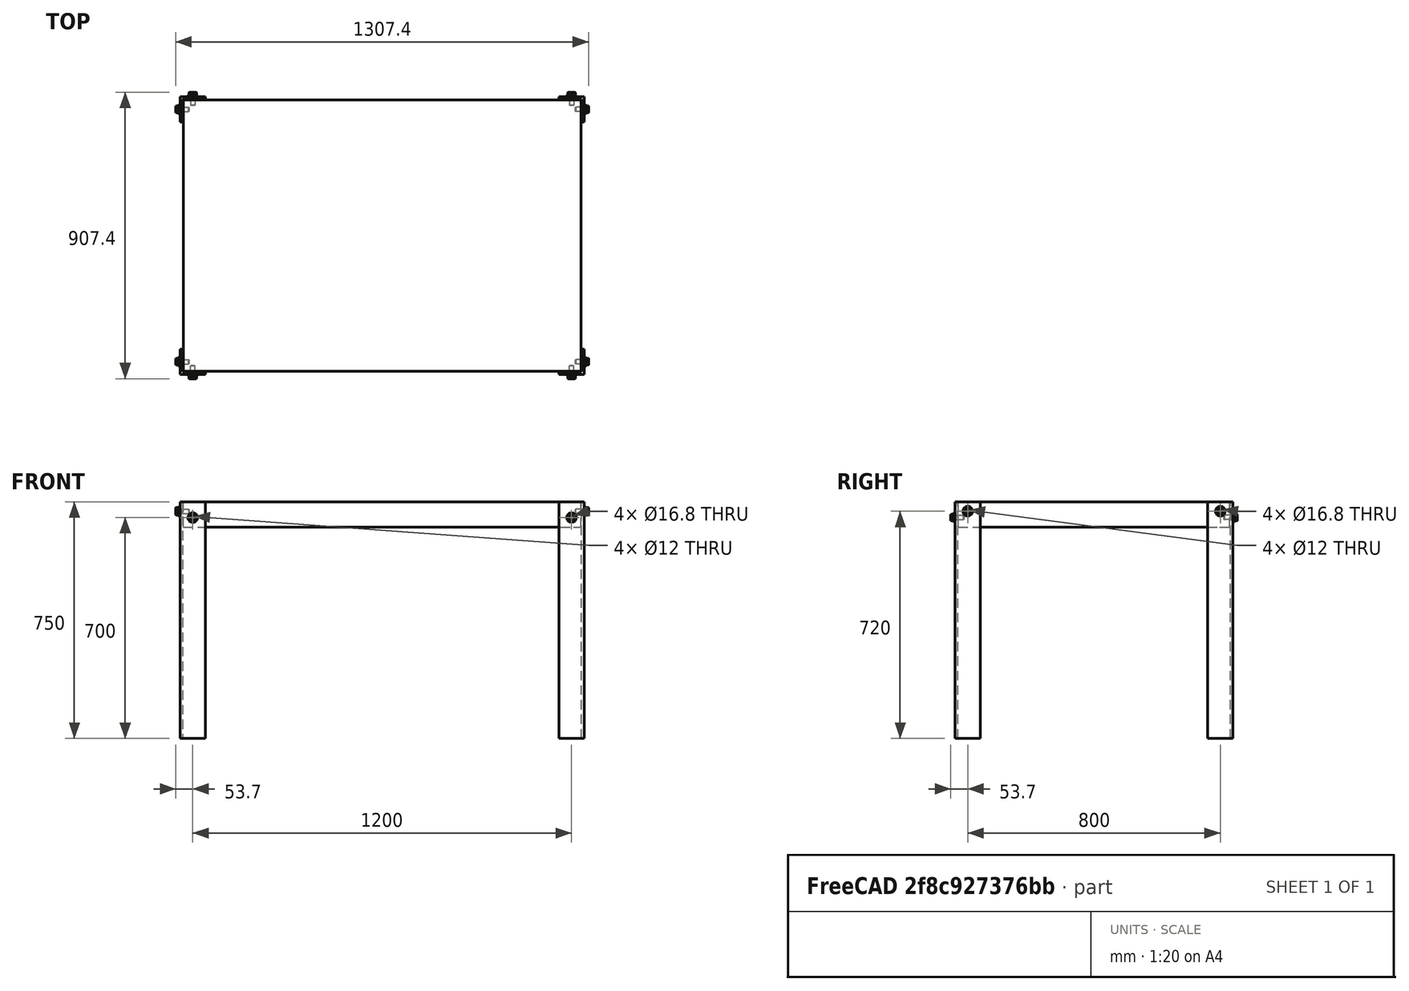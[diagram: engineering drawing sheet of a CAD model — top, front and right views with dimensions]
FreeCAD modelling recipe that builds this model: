
FCSTD DOCUMENT  (FreeCAD 0.17R13519 (Git))
Label: test005_table
License: All rights reserved
LicenseURL: http://en.wikipedia.org/wiki/All_rights_reserved
objects: Part::Cut×12, Part::Box×9, Part::FeaturePython×8, Part::Cylinder×4, App::DocumentObjectGroup×1
note: 33 computed .brp shape members not serialized (recipe doc carries the construction recipe); baked Part::Feature solids carry a one-line shape summary decoded from their .brp

FEATURE [Part::Box] Box  label="Cube"
  AttacherType = Attacher::AttachEngine3D
  Height = 750
  Length = 80
  Width = 80
FEATURE [Part::Box] Box001  label="Cube001"
  AttacherType = Attacher::AttachEngine3D
  Height = 750
  Length = 80
  Placement = pos=(8,8,0) rot=(0,0,1;0rad)
  Width = 80
FEATURE [Part::Cut] Cut
  Base = -> Box
  Tool = -> Box001
FEATURE [Part::Box] Box002  label="Cube002"
  AttacherType = Attacher::AttachEngine3D
  Height = 750
  Length = 80
  Placement = pos=(0,800,0) rot=(0,0,1;0rad)
  Width = 80
FEATURE [Part::Box] Box003  label="Cube003"
  AttacherType = Attacher::AttachEngine3D
  Height = 750
  Length = 80
  Placement = pos=(8,792,0) rot=(0,0,1;0rad)
  Width = 80
FEATURE [Part::Cut] Cut001
  Base = -> Box002
  Tool = -> Box003
FEATURE [Part::Box] Box004  label="Cube004"
  AttacherType = Attacher::AttachEngine3D
  Height = 750
  Length = 80
  Placement = pos=(1200,0,0) rot=(0,0,1;0rad)
  Width = 80
FEATURE [Part::Box] Box005  label="Cube005"
  AttacherType = Attacher::AttachEngine3D
  Height = 750
  Length = 80
  Placement = pos=(1192,8,0) rot=(0,0,1;0rad)
  Width = 80
FEATURE [Part::Cut] Cut002
  Base = -> Box004
  Tool = -> Box005
FEATURE [Part::Box] Box006  label="Cube006"
  AttacherType = Attacher::AttachEngine3D
  Height = 750
  Length = 80
  Placement = pos=(1200,800,0) rot=(0,0,1;0rad)
  Width = 80
FEATURE [Part::Box] Box007  label="Cube007"
  AttacherType = Attacher::AttachEngine3D
  Height = 750
  Length = 80
  Placement = pos=(1192,792,0) rot=(0,0,1;0rad)
  Width = 80
FEATURE [Part::Cut] Cut003
  Base = -> Box006
  Tool = -> Box007
FEATURE [Part::Cylinder] Cylinder
  Angle = 360
  AttacherType = Attacher::AttachEngine3D
  Height = 1300
  Placement = pos=(-10,40,720) rot=(0,1,0;1.5708rad)
  Radius = 6
FEATURE [Part::Cylinder] Cylinder001
  Angle = 360
  AttacherType = Attacher::AttachEngine3D
  Height = 1300
  Placement = pos=(-10,840,720) rot=(0,1,0;1.5708rad)
  Radius = 6
FEATURE [Part::Cylinder] Cylinder002
  Angle = 360
  AttacherType = Attacher::AttachEngine3D
  Height = 900
  Placement = pos=(40,-10,700) rot=(-1,0,0;1.5708rad)
  Radius = 6
FEATURE [Part::Cylinder] Cylinder003
  Angle = 360
  AttacherType = Attacher::AttachEngine3D
  Height = 900
  Placement = pos=(1240,-10,700) rot=(-1,0,0;1.5708rad)
  Radius = 6
FEATURE [Part::Cut] Cut004
  Base = -> Cut
  Tool = -> Cylinder
FEATURE [Part::Cut] Cut005
  Base = -> Cut002
  Tool = -> Cylinder
FEATURE [Part::Cut] Cut006
  Base = -> Cut001
  Tool = -> Cylinder001
FEATURE [Part::Cut] Cut007  label="LeftBackLeg"
  Base = -> Cut006
  Tool = -> Cylinder002
FEATURE [Part::Cut] Cut008  label="RightFrontLeg"
  Base = -> Cut005
  Tool = -> Cylinder003
FEATURE [Part::Cut] Cut009
  Base = -> Cut003
  Tool = -> Cylinder003
FEATURE [Part::Cut] Cut010  label="RightBackLeg"
  Base = -> Cut009
  Tool = -> Cylinder001
FEATURE [Part::Cut] Cut011  label="LeftFrontLeg"
  Base = -> Cut004
  Tool = -> Cylinder002
FEATURE [Part::Box] Box008  label="Table"
  AttacherType = Attacher::AttachEngine3D
  Height = 80
  Length = 1260
  Placement = pos=(10,10,670) rot=(0,0,1;0rad)
  Width = 860
FEATURE [Part::FeaturePython] Screw  label="(M14)x30-Screw"  # Fasteners workbench fastener (typed FeaturePython)
  Placement = pos=(40,-2,700) rot=(1,0,0;1.5708rad)
  baseObject = -> Cut011 [Edge9]
  diameter = 6
  invert = true
  length = 0
  matchOuter = false
  offset = 2
  thread = false
  type = 2
FEATURE [Part::FeaturePython] Screw001  label="(M14)x30-Screw001"  # Fasteners workbench fastener (typed FeaturePython)
  Placement = pos=(-2,40,720) rot=(0,-1,0;1.5708rad)
  baseObject = -> Cut011 [Edge5]
  diameter = 6
  invert = true
  length = 0
  matchOuter = false
  offset = 2
  thread = false
  type = 2
FEATURE [Part::FeaturePython] Screw002  label="(M14)x30-Screw003"  # Fasteners workbench fastener (typed FeaturePython)
  Placement = pos=(-2,840,720) rot=(0,-1,0;1.5708rad)
  baseObject = -> Cut007 [Edge5]
  diameter = 6
  invert = true
  length = 0
  matchOuter = false
  offset = 2
  thread = false
  type = 2
FEATURE [Part::FeaturePython] Screw003  label="(M14)x30-Screw004"  # Fasteners workbench fastener (typed FeaturePython)
  Placement = pos=(40,882,700) rot=(-1,0,0;1.5708rad)
  baseObject = -> Cut007 [Edge18]
  diameter = 6
  invert = false
  length = 0
  matchOuter = false
  offset = 2
  thread = false
  type = 2
FEATURE [Part::FeaturePython] Screw004  label="(M14)x30-Screw010"  # Fasteners workbench fastener (typed FeaturePython)
  Placement = pos=(1240,882,700) rot=(-1,0,0;1.5708rad)
  baseObject = -> Cut010 [Edge12]
  diameter = 6
  invert = false
  length = 0
  matchOuter = false
  offset = 2
  thread = false
  type = 2
FEATURE [Part::FeaturePython] Screw005  label="(M14)x30-Screw011"  # Fasteners workbench fastener (typed FeaturePython)
  Placement = pos=(1282,840,720) rot=(0,1,0;1.5708rad)
  baseObject = -> Cut010 [Edge20]
  diameter = 6
  invert = false
  length = 0
  matchOuter = false
  offset = 2
  thread = false
  type = 2
FEATURE [Part::FeaturePython] Screw006  label="(M14)x30-Screw009"  # Fasteners workbench fastener (typed FeaturePython)
  Placement = pos=(1282,40,720) rot=(0,1,0;1.5708rad)
  baseObject = -> Cut008 [Edge22]
  diameter = 6
  invert = false
  length = 0
  matchOuter = false
  offset = 2
  thread = false
  type = 2
FEATURE [Part::FeaturePython] Screw007  label="(M14)x30-Screw008"  # Fasteners workbench fastener (typed FeaturePython)
  Placement = pos=(1240,-2,700) rot=(1,0,0;1.5708rad)
  baseObject = -> Cut008 [Edge18]
  diameter = 6
  invert = true
  length = 0
  matchOuter = false
  offset = 2
  thread = false
  type = 2
FEATURE [App::DocumentObjectGroup] Group  label="Screws"
  Group = -> [Screw,Screw001,Screw002,Screw003,Screw004,Screw005,Screw006,Screw007]
